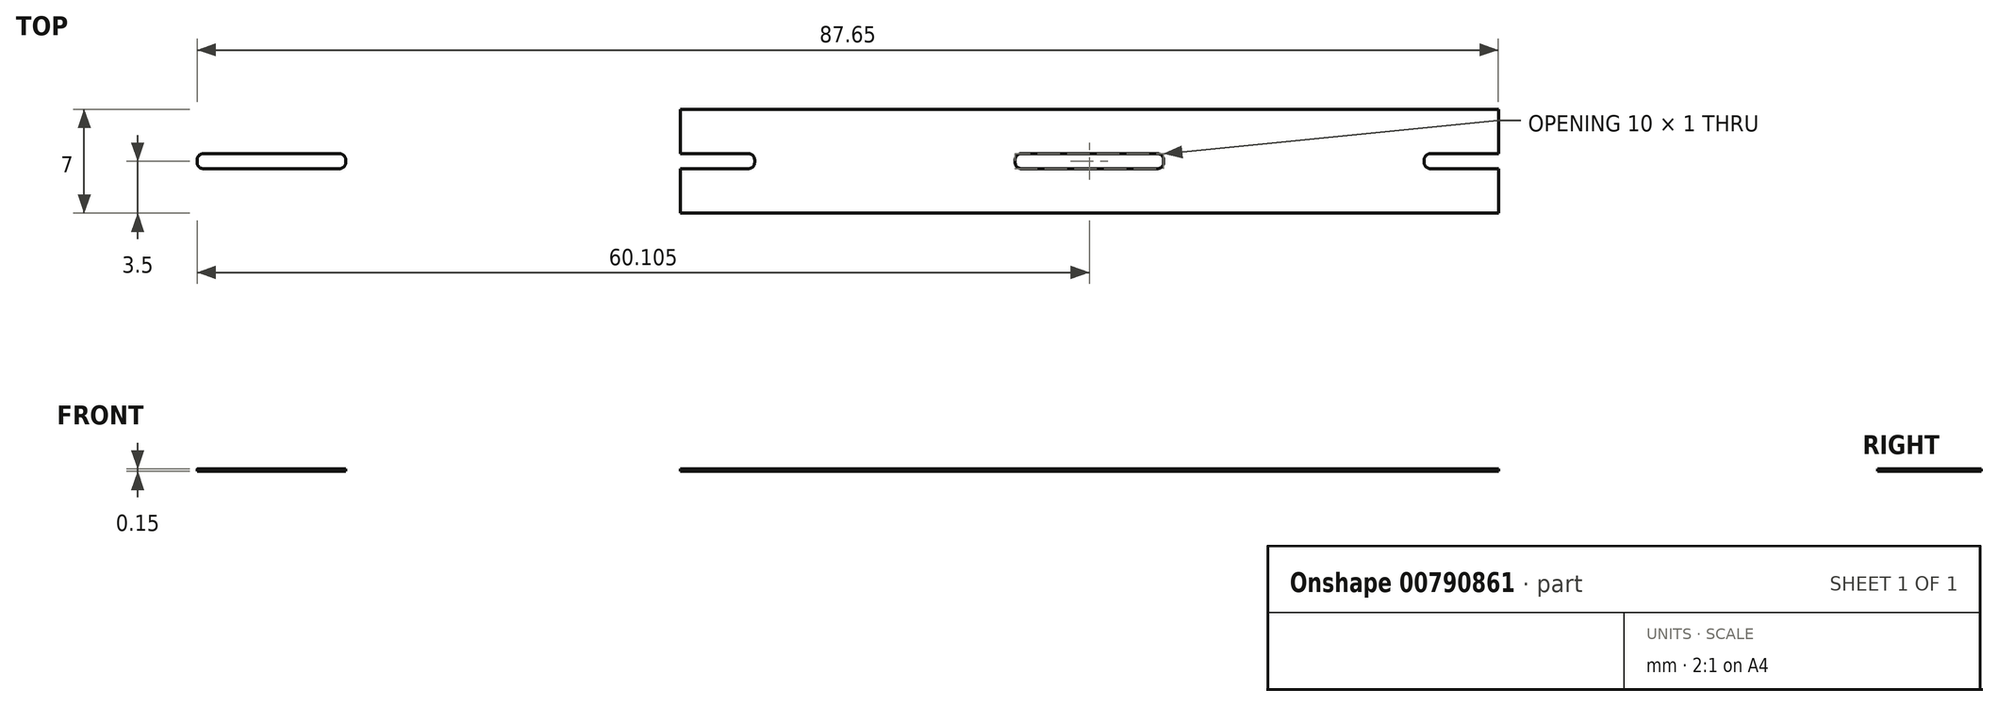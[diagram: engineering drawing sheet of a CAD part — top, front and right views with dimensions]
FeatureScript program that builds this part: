
annotation { "Feature Type Name" : "Feature", "Feature Type Description" : "" }
export const myFeature = defineFeature(function(context is Context, id is Id, definition is map)
    precondition{}
    {
        {
            var Q0;
            Q0=qCreatedBy(makeId("Top.planeOp"),FACE);
            var sketch = newSketch(context, id + "F0", { "sketchPlane" : qUnion([Q0])});
            skPoint(sketch, "E0.middle", {"position": v(0, 0) * mm});
            skLineSegment(sketch, "E1.bottom", {"start": v(-9.18, -0.5) * mm, "end": v(-13.78, -0.5) * mm});
            skLineSegment(sketch, "E1.top", {"start": v(-9.18, 0.5) * mm, "end": v(-13.78, 0.5) * mm});
            skLineSegment(sketch, "E1.left", {"start": v(-8.78, -0.1) * mm, "end": v(-8.78, 0.1) * mm});
            skLineSegment(sketch, "E1.right", {"start": v(-18.78, -0.1) * mm, "end": v(-18.78, 0.1) * mm});
            skPoint(sketch, "E1.middle", {"position": v(-13.78, 0) * mm});
            skPoint(sketch, "E2.visualSharp", {"position": v(-8.78, 0.5) * mm});
            skArc(sketch, "E2.filletArc", {"start": v(-8.78, 0.1) * mm, "mid": v(-8.9, 0.38) * mm, "end": v(-9.18, 0.5) * mm});
            skPoint(sketch, "E3.visualSharp", {"position": v(-8.78, -0.5) * mm});
            skArc(sketch, "E3.filletArc", {"start": v(-9.18, -0.5) * mm, "mid": v(-8.9, -0.38) * mm, "end": v(-8.78, -0.1) * mm});
            skPoint(sketch, "E4.visualSharp", {"position": v(-18.78, 0.5) * mm});
            skArc(sketch, "E4.filletArc", {"start": v(-18.38, 0.5) * mm, "mid": v(-18.66, 0.38) * mm, "end": v(-18.77, 0.1) * mm});
            skPoint(sketch, "E5.visualSharp", {"position": v(-18.78, -0.5) * mm});
            skArc(sketch, "E5.filletArc", {"start": v(-18.77, -0.1) * mm, "mid": v(-18.66, -0.38) * mm, "end": v(-18.38, -0.5) * mm});
            skLineSegment(sketch, "E6", {"start": v(0, 3.5) * mm, "end": v(-13.78, 3.5) * mm});
            skPoint(sketch, "E6.endSnap0", {"position": v(-13.78, 0.5) * mm});
            skLineSegment(sketch, "E7", {"start": v(-13.78, 3.5) * mm, "end": v(-13.78, 0.5) * mm});
            skLineSegment(sketch, "E8.MirrorCS", {"start": v(0, -3.5) * mm, "end": v(-13.78, -3.5) * mm});
            skLineSegment(sketch, "E9.MirrorCS", {"start": v(-13.78, -3.5) * mm, "end": v(-13.78, -0.5) * mm});
            skLineSegment(sketch, "E10.MirrorCS", {"start": v(0, 3.5) * mm, "end": v(13.78, 3.5) * mm});
            skLineSegment(sketch, "E11.MirrorCS", {"start": v(0, -3.5) * mm, "end": v(13.78, -3.5) * mm});
            skLineSegment(sketch, "E12.MirrorCS", {"start": v(8.78, -0.1) * mm, "end": v(8.78, 0.1) * mm});
            skArc(sketch, "E13.MirrorCS", {"start": v(8.78, 0.1) * mm, "mid": v(8.9, 0.38) * mm, "end": v(9.18, 0.5) * mm});
            skArc(sketch, "E14.MirrorCS", {"start": v(18.77, -0.1) * mm, "mid": v(18.66, -0.38) * mm, "end": v(18.38, -0.5) * mm});
            skLineSegment(sketch, "E15.MirrorCS", {"start": v(18.78, -0.1) * mm, "end": v(18.78, 0.1) * mm});
            skArc(sketch, "E16.MirrorCS", {"start": v(18.38, 0.5) * mm, "mid": v(18.66, 0.38) * mm, "end": v(18.77, 0.1) * mm});
            skArc(sketch, "E17.MirrorCS", {"start": v(9.18, -0.5) * mm, "mid": v(8.9, -0.38) * mm, "end": v(8.78, -0.1) * mm});
            skPoint(sketch, "E18.MirrorP", {"position": v(18.78, 0.5) * mm});
            skLineSegment(sketch, "E19.MirrorCS", {"start": v(9.18, 0.5) * mm, "end": v(18.38, 0.5) * mm});
            skLineSegment(sketch, "E20.MirrorCS", {"start": v(9.18, -0.5) * mm, "end": v(18.38, -0.5) * mm});
            skPoint(sketch, "E21.MirrorP", {"position": v(13.78, 0.5) * mm});
            skPoint(sketch, "E22.MirrorP", {"position": v(8.78, 0.5) * mm});
            skPoint(sketch, "E23.MirrorP", {"position": v(18.78, -0.5) * mm});
            skPoint(sketch, "E24.MirrorP", {"position": v(8.78, -0.5) * mm});
            skPoint(sketch, "E25.MirrorP", {"position": v(13.78, 0) * mm});
            skLineSegment(sketch, "E26.MirrorCS", {"start": v(13.78, 3.5) * mm, "end": v(13.78, 0.5) * mm});
            skLineSegment(sketch, "E27.MirrorCS", {"start": v(13.78, -3.5) * mm, "end": v(13.78, -0.5) * mm});
            skPoint(sketch, "E28.1.0.0", {"position": v(36.33, 0.5) * mm});
            skLineSegment(sketch, "E28.1.0.1", {"start": v(27.55, 3.5) * mm, "end": v(41.33, 3.5) * mm});
            skLineSegment(sketch, "E28.1.0.2", {"start": v(36.73, -0.5) * mm, "end": v(45.92, -0.5) * mm});
            skPoint(sketch, "E28.1.0.3", {"position": v(27.55, 0) * mm});
            skLineSegment(sketch, "E28.1.0.4", {"start": v(27.55, -3.5) * mm, "end": v(41.33, -3.5) * mm});
            skPoint(sketch, "E28.1.0.5", {"position": v(41.33, 0.5) * mm});
            skPoint(sketch, "E28.1.0.6", {"position": v(41.33, 0) * mm});
            skPoint(sketch, "E28.1.0.7", {"position": v(46.33, -0.5) * mm});
            skPoint(sketch, "E28.1.0.8", {"position": v(36.33, -0.5) * mm});
            skLineSegment(sketch, "E28.1.0.9", {"start": v(27.55, -3.5) * mm, "end": v(13.77, -3.5) * mm});
            skLineSegment(sketch, "E28.1.0.10", {"start": v(36.73, 0.5) * mm, "end": v(45.92, 0.5) * mm});
            skLineSegment(sketch, "E28.1.0.11", {"start": v(27.55, 3.5) * mm, "end": v(13.77, 3.5) * mm});
            skLineSegment(sketch, "E28.1.0.12", {"start": v(41.33, 3.5) * mm, "end": v(41.33, 0.5) * mm});
            skLineSegment(sketch, "E28.1.0.13", {"start": v(41.33, -3.5) * mm, "end": v(41.33, -0.5) * mm});
            skPoint(sketch, "E28.1.0.14", {"position": v(46.33, 0.5) * mm});
            skArc(sketch, "E28.1.0.15", {"start": v(45.92, 0.5) * mm, "mid": v(46.2, 0.38) * mm, "end": v(46.32, 0.1) * mm});
            skArc(sketch, "E28.1.0.16", {"start": v(36.73, -0.5) * mm, "mid": v(36.44, -0.38) * mm, "end": v(36.33, -0.1) * mm});
            skArc(sketch, "E28.1.0.17", {"start": v(46.32, -0.1) * mm, "mid": v(46.2, -0.38) * mm, "end": v(45.92, -0.5) * mm});
            skArc(sketch, "E28.1.0.18", {"start": v(36.33, 0.1) * mm, "mid": v(36.44, 0.38) * mm, "end": v(36.73, 0.5) * mm});
            skLineSegment(sketch, "E28.1.0.19", {"start": v(36.33, -0.1) * mm, "end": v(36.33, 0.1) * mm});
            skLineSegment(sketch, "E28.1.0.20", {"start": v(46.33, -0.1) * mm, "end": v(46.33, 0.1) * mm});
            skPoint(sketch, "E28.2.0.0", {"position": v(63.88, 0.5) * mm});
            skLineSegment(sketch, "E28.2.0.1", {"start": v(55.1, 3.5) * mm, "end": v(68.88, 3.5) * mm});
            skLineSegment(sketch, "E28.2.0.2", {"start": v(64.28, -0.5) * mm, "end": v(73.47, -0.5) * mm});
            skPoint(sketch, "E28.2.0.3", {"position": v(55.1, 0) * mm});
            skLineSegment(sketch, "E28.2.0.4", {"start": v(55.1, -3.5) * mm, "end": v(68.88, -3.5) * mm});
            skPoint(sketch, "E28.2.0.5", {"position": v(68.88, 0.5) * mm});
            skPoint(sketch, "E28.2.0.6", {"position": v(68.87, 0) * mm});
            skPoint(sketch, "E28.2.0.7", {"position": v(73.88, -0.5) * mm});
            skPoint(sketch, "E28.2.0.8", {"position": v(63.88, -0.5) * mm});
            skLineSegment(sketch, "E28.2.0.9", {"start": v(55.1, -3.5) * mm, "end": v(41.32, -3.5) * mm});
            skLineSegment(sketch, "E28.2.0.10", {"start": v(64.28, 0.5) * mm, "end": v(73.47, 0.5) * mm});
            skLineSegment(sketch, "E28.2.0.11", {"start": v(55.1, 3.5) * mm, "end": v(41.32, 3.5) * mm});
            skLineSegment(sketch, "E28.2.0.12", {"start": v(68.87, 3.5) * mm, "end": v(68.87, 0.5) * mm});
            skLineSegment(sketch, "E28.2.0.13", {"start": v(68.87, -3.5) * mm, "end": v(68.87, -0.5) * mm});
            skPoint(sketch, "E28.2.0.14", {"position": v(73.88, 0.5) * mm});
            skArc(sketch, "E28.2.0.15", {"start": v(73.47, 0.5) * mm, "mid": v(73.76, 0.38) * mm, "end": v(73.88, 0.1) * mm});
            skArc(sketch, "E28.2.0.16", {"start": v(64.28, -0.5) * mm, "mid": v(64, -0.38) * mm, "end": v(63.88, -0.1) * mm});
            skArc(sketch, "E28.2.0.17", {"start": v(73.88, -0.1) * mm, "mid": v(73.76, -0.38) * mm, "end": v(73.47, -0.5) * mm});
            skArc(sketch, "E28.2.0.18", {"start": v(63.88, 0.1) * mm, "mid": v(64, 0.38) * mm, "end": v(64.28, 0.5) * mm});
            skLineSegment(sketch, "E28.2.0.19", {"start": v(63.88, -0.1) * mm, "end": v(63.88, 0.1) * mm});
            skLineSegment(sketch, "E28.2.0.20", {"start": v(73.88, -0.1) * mm, "end": v(73.88, 0.1) * mm});
            skPoint(sketch, "E28.3.0.0", {"position": v(91.43, 0.5) * mm});
            skLineSegment(sketch, "E28.3.0.1", {"start": v(82.65, 3.5) * mm, "end": v(96.43, 3.5) * mm});
            skLineSegment(sketch, "E28.3.0.2", {"start": v(91.83, -0.5) * mm, "end": v(101.03, -0.5) * mm});
            skPoint(sketch, "E28.3.0.3", {"position": v(82.65, 0) * mm});
            skLineSegment(sketch, "E28.3.0.4", {"start": v(82.65, -3.5) * mm, "end": v(96.43, -3.5) * mm});
            skPoint(sketch, "E28.3.0.5", {"position": v(96.43, 0.5) * mm});
            skPoint(sketch, "E28.3.0.6", {"position": v(96.42, 0) * mm});
            skPoint(sketch, "E28.3.0.7", {"position": v(101.42, -0.5) * mm});
            skPoint(sketch, "E28.3.0.8", {"position": v(91.43, -0.5) * mm});
            skLineSegment(sketch, "E28.3.0.9", {"start": v(82.65, -3.5) * mm, "end": v(68.87, -3.5) * mm});
            skLineSegment(sketch, "E28.3.0.10", {"start": v(91.83, 0.5) * mm, "end": v(101.03, 0.5) * mm});
            skLineSegment(sketch, "E28.3.0.11", {"start": v(82.65, 3.5) * mm, "end": v(68.87, 3.5) * mm});
            skLineSegment(sketch, "E28.3.0.12", {"start": v(96.43, 3.5) * mm, "end": v(96.43, 0.5) * mm});
            skLineSegment(sketch, "E28.3.0.13", {"start": v(96.43, -3.5) * mm, "end": v(96.43, -0.5) * mm});
            skPoint(sketch, "E28.3.0.14", {"position": v(101.42, 0.5) * mm});
            skArc(sketch, "E28.3.0.15", {"start": v(101.03, 0.5) * mm, "mid": v(101.3, 0.38) * mm, "end": v(101.42, 0.1) * mm});
            skArc(sketch, "E28.3.0.16", {"start": v(91.83, -0.5) * mm, "mid": v(91.54, -0.38) * mm, "end": v(91.43, -0.1) * mm});
            skArc(sketch, "E28.3.0.17", {"start": v(101.42, -0.1) * mm, "mid": v(101.3, -0.38) * mm, "end": v(101.03, -0.5) * mm});
            skArc(sketch, "E28.3.0.18", {"start": v(91.43, 0.1) * mm, "mid": v(91.54, 0.38) * mm, "end": v(91.83, 0.5) * mm});
            skLineSegment(sketch, "E28.3.0.19", {"start": v(91.43, -0.1) * mm, "end": v(91.43, 0.1) * mm});
            skLineSegment(sketch, "E28.3.0.20", {"start": v(101.42, -0.1) * mm, "end": v(101.42, 0.1) * mm});
            skLineSegment(sketch, "E28.direction1", {"start": v(-13.78, -3.5) * mm, "end": v(13.77, -3.5) * mm, "construction": true});
            skLineSegment(sketch, "E29", {"start": v(0, 3.5) * mm, "end": v(0, -3.5) * mm});
            skSolve(sketch);
        }
        {
            var Q0;
            {var subQ8=sQuery(id+"F0.wireOp",EDGE,"E28.3.0.12");Q0=makeQuery(id+"F0.imprint","IMPRINT",FACE,{"disambiguationData":[TD([[makeQuery(id+"F0.imprint","IMPRINT",EDGE,{"derivedFrom":subQ8}),1.0]])]});}
            var Q1;
            {var subQ3=sQuery(id+"F0.wireOp",EDGE,"E14.MirrorCS");Q1=makeQuery(id+"F0.imprint","IMPRINT",FACE,{"disambiguationData":[TD([[makeQuery(id+"F0.imprint","IMPRINT",EDGE,{"derivedFrom":subQ3}),1.0]])]});}
            var Q2;
            {var subQ8=sQuery(id+"F0.wireOp",EDGE,"E28.1.0.12");Q2=makeQuery(id+"F0.imprint","IMPRINT",FACE,{"disambiguationData":[TD([[makeQuery(id+"F0.imprint","IMPRINT",EDGE,{"derivedFrom":subQ8}),1.0]])]});}
            var Q3;
            {var subQ8=sQuery(id+"F0.wireOp",EDGE,"E28.2.0.12");Q3=makeQuery(id+"F0.imprint","IMPRINT",FACE,{"disambiguationData":[TD([[makeQuery(id+"F0.imprint","IMPRINT",EDGE,{"derivedFrom":subQ8}),1.0]])]});}
            extrude(context, id + "F1", {"entities" : qUnion([Q0, Q1, Q2, Q3]), "depth" : 0.15 * mm, "offsetDistance" : 25 * mm});
        }
    });
